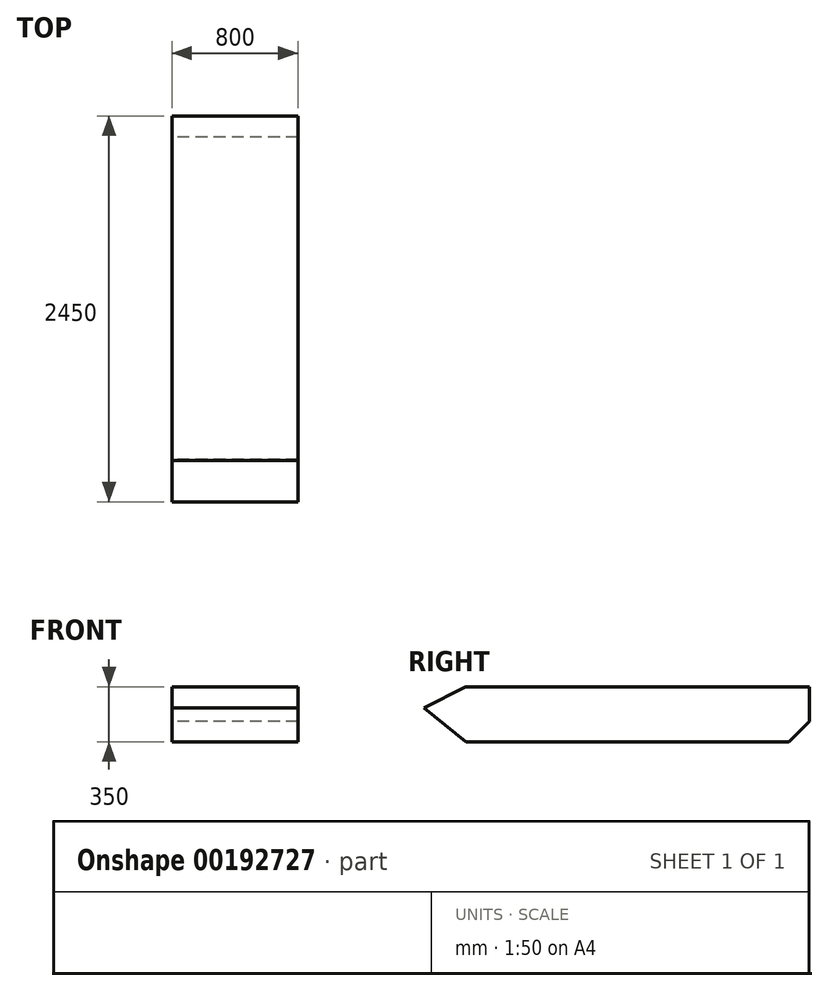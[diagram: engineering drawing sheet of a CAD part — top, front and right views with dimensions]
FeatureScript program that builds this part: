
annotation { "Feature Type Name" : "Feature", "Feature Type Description" : "" }
export const myFeature = defineFeature(function(context is Context, id is Id, definition is map)
    precondition{}
    {
        {
            var Q0;
            Q0=qCreatedBy(makeId("Right.planeOp"),FACE);
            var sketch = newSketch(context, id + "F0", { "sketchPlane" : qUnion([Q0])});
            skLineSegment(sketch, "E0.bottom", {"start": v(1225, -175) * mm, "end": v(-1225, -175) * mm});
            skLineSegment(sketch, "E0.top", {"start": v(1225, 175) * mm, "end": v(-1225, 175) * mm});
            skLineSegment(sketch, "E0.left", {"start": v(1225, -175) * mm, "end": v(1225, 175) * mm});
            skLineSegment(sketch, "E0.right", {"start": v(-1225, -175) * mm, "end": v(-1225, 175) * mm});
            skPoint(sketch, "E0.middle", {"position": v(0, 0) * mm});
            skLineSegment(sketch, "E1", {"start": v(-1225, 42) * mm, "end": v(-962.09, 175) * mm});
            skLineSegment(sketch, "E2", {"start": v(-1225, 42) * mm, "end": v(-957, -175) * mm});
            skLineSegment(sketch, "E3", {"start": v(1225, -45) * mm, "end": v(1092, -175) * mm});
            skSolve(sketch);
        }
        {
            var Q0;
            {var subQ0=sQuery(id+"F0.wireOp",EDGE,"E1");Q0=makeQuery(id+"F0.imprint","IMPRINT",FACE,{"disambiguationData":[TD([[makeQuery(id+"F0.imprint","IMPRINT",EDGE,{"derivedFrom":subQ0}),-1.0]])]});}
            extrude(context, id + "F1", {"entities" : qUnion([Q0]), "depth" : 400 * mm, "hasSecondDirection" : true, "secondDirectionOppositeDirection" : true, "secondDirectionDepth" : 400 * mm});
        }
    });
